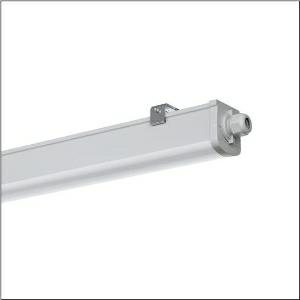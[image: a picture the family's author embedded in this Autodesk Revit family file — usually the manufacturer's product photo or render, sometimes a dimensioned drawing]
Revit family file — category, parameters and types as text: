
# Revit family: monsun_r__31_51fa207p460b_ddf4
name_source: partatom
category: Lighting Fixtures
units: mm (PartAtom-declared; Revit-internal decimal feet)

## family parameters
Cut with Voids When Loaded = No
Host = Face
Light Source = No
Part Type = Normal
Room Calculation Point = No
Round Connector Dimension = Use Diameter
Shared = No

## types (1)
- Monsun® 31 (1 x LED, 6700 lm, 50 W, 4000K)
    Apparent Load = 50 VA
    CIE Flux Codes = 42 72 91 92 100
    Color Rendering = 80
    Color Temperature = 4000K
    Default Elevation = 1800 mm
    Description = Monsun® 31, damp-proof luminaire, primary optical cover: diffuser, of PC, frosted, light emission: direct distribution, primary light characteristic: symmetric, installation type: surface-mounted, LED, rated luminous flux: 6.700lm, luminous efficacy: 134lm/W, light colour: 840, colour temperature: 4000K, control gear: ON/OFF, with terminal, 3+1-pole, max. 2.5mm², through-wiring: 3x 2.5mm² + 1x 1.5mm², mains connection: 220..240V, AC, 50/60Hz, rated input power: 50W, housing, luminaire housing, of PC, light grey (RAL 7035), length: 1.458mm, width: 68mm, height: 76mm, protection rating (complete): IP66, insulation class (complete): insulation class II (safety insulation), certification: CE, ENEC, UKCA, protection symbol: D, impact resistance: IK08, permissible operating ambient temperature: -20..+40°C, corresponds to IFS (International Featured Standards) requirements for safety and quality in the food industry, contact your sales advisor before using the luminaires in applications with unclear chemical exposure, large temperature fluctuations or condensation-forming humidity, packaging unit: 1 piece
    Height = 77 mm
    Lamp = 1 x LED
    Lamp Light Flux = 6700 lm
    Lamp Power = 50 W
    Lamp count = 1
    Length = 1518 mm
    Luminous efficacy = 134 lm/W
    Manufacturer = Siteco
    ModVariant = No
    Model = 51FA207P460B
    Mounting Place = Ceiling
    Mounting Type = Surface mounted
    Number of Poles = 1
    OnlyDefault = Yes
    Power Factor = 1
    Product Name = Monsun® 31
    Product group = damp-proof luminaire
    ProductGroupID = 300
    Protection Class = Protection class II
    Protection Degree = IP 66
    RLX_Detail_Level = 1
    RLX_Emergency_Light_Flux = 0 lm
    RLX_Emergency_Type = 0
    RLX_Emergency_Type_DB = No
    RlxData = <blob elided: 33077 chars, md5=181b8bcf>
    Socket = socket
    Standby Power = 0 W
    System Light Flux = 6700 lm
    System Power = 50 W
    Type Comments = Product without accessories
    Type Image = l_1006174.jpg
    URL = http://relux.com
    VarID = ---
    Voltage = 0 V
    Weight = 0.00 kg
    Width = 69 mm

## geometry (parser evidence)
native form markers: Blend x4, Sweep x12
no freeform markers — native parametric forms only
